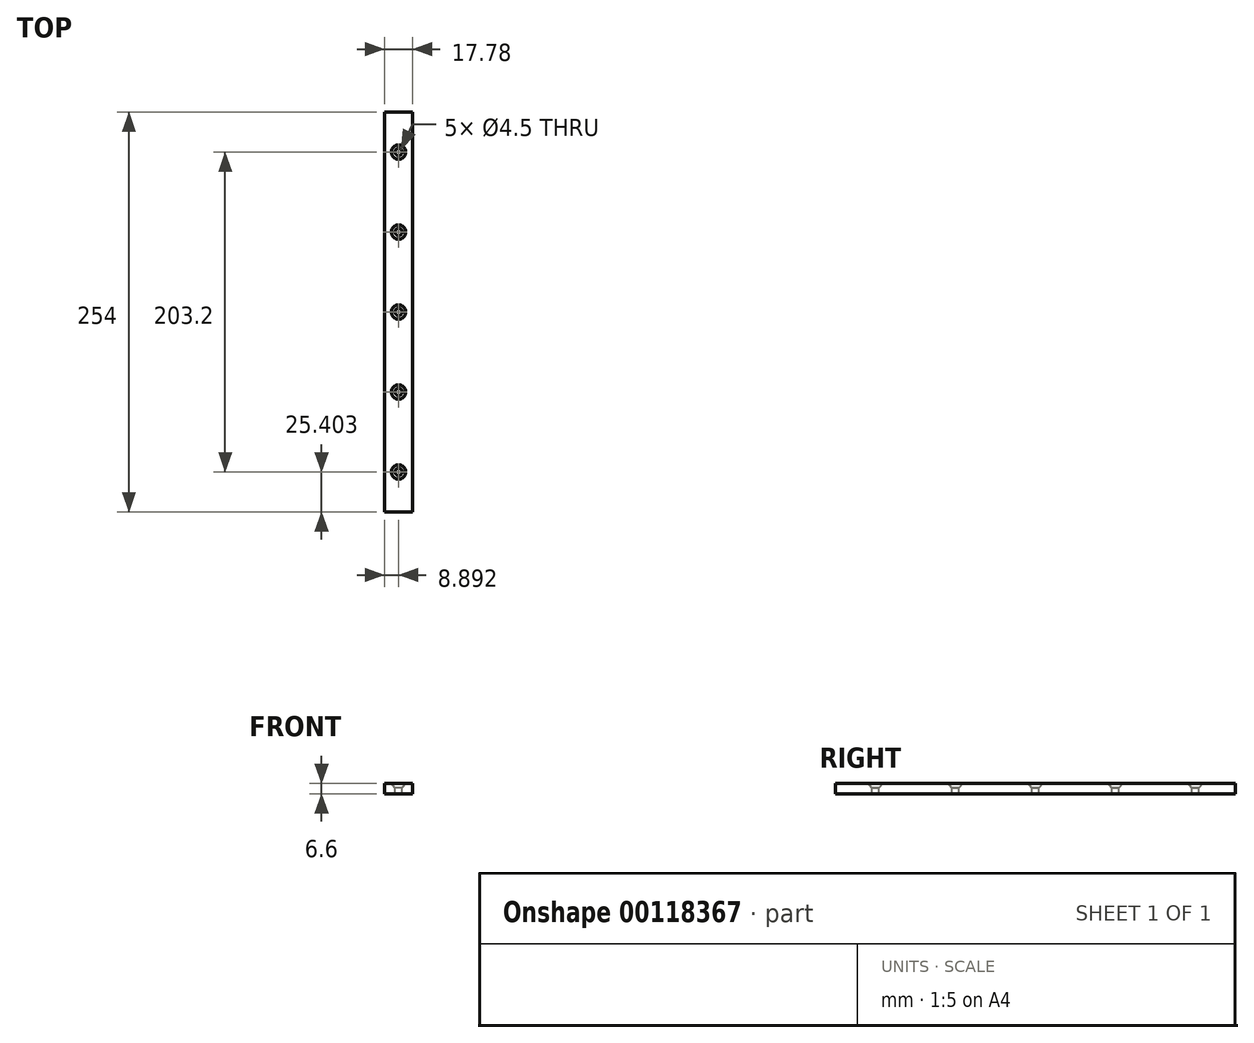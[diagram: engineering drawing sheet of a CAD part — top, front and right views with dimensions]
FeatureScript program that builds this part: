
annotation { "Feature Type Name" : "Feature", "Feature Type Description" : "" }
export const myFeature = defineFeature(function(context is Context, id is Id, definition is map)
    precondition{}
    {
        {
            var Q0;
            Q0=qCreatedBy(makeId("Top.planeOp"),FACE);
            var sketch = newSketch(context, id + "F0", { "sketchPlane" : qUnion([Q0])});
            skLineSegment(sketch, "E0.bottom", {"start": v(-5.89, 167.12) * mm, "end": v(11.9, 167.12) * mm});
            skLineSegment(sketch, "E0.top", {"start": v(-5.89, -86.88) * mm, "end": v(11.9, -86.88) * mm});
            skLineSegment(sketch, "E0.left", {"start": v(-5.89, 167.12) * mm, "end": v(-5.89, -86.88) * mm});
            skLineSegment(sketch, "E0.right", {"start": v(11.9, 167.12) * mm, "end": v(11.9, -86.88) * mm});
            skPoint(sketch, "E1.cCircle.centerSnap0", {"position": v(3, 167.12) * mm});
            skPoint(sketch, "E2.0.midPoint", {"position": v(5.8, 105.13) * mm});
            skSolve(sketch);
        }
        {
            var Q0;
            Q0=makeQuery(id+"F0.imprint","IMPRINT",FACE,{"disambiguationData":[TD([[makeQuery(id+"F0.imprint","IMPRINT",EDGE,{"derivedFrom":sQuery(id+"F0.wireOp",EDGE,"E0.bottom")}),-1.0]])]});
            extrude(context, id + "F1", {"entities" : qUnion([Q0]), "depth" : 6.6 * mm});
        }
        {
            var Q0;
            Q0=makeQuery(id+"F1.opExtrude","CAP_FACE",FACE,{"disambiguationData":[OSD([sQuery(id+"F0.wireOp",EDGE,"E0.bottom"),sQuery(id+"F0.wireOp",EDGE,"E0.top"),sQuery(id+"F0.wireOp",EDGE,"E0.left"),sQuery(id+"F0.wireOp",EDGE,"E0.right"),sQuery(id+"F0.wireOp",EDGE,"E1.0"),sQuery(id+"F0.wireOp",EDGE,"E1.1"),sQuery(id+"F0.wireOp",EDGE,"E1.2"),sQuery(id+"F0.wireOp",EDGE,"E1.3"),sQuery(id+"F0.wireOp",EDGE,"E1.4"),sQuery(id+"F0.wireOp",EDGE,"E1.5"),sQuery(id+"F0.wireOp",EDGE,"E2.0"),sQuery(id+"F0.wireOp",EDGE,"E2.1"),sQuery(id+"F0.wireOp",EDGE,"E2.2"),sQuery(id+"F0.wireOp",EDGE,"E2.3"),sQuery(id+"F0.wireOp",EDGE,"E2.4"),sQuery(id+"F0.wireOp",EDGE,"E2.5")])],"isStart":false});
            var sketch = newSketch(context, id + "F2", { "sketchPlane" : qUnion([Q0])});
            skPoint(sketch, "E3", {"position": v(3, -61.48) * mm});
            skPoint(sketch, "E3.positionSnap0", {"position": v(3, -86.88) * mm});
            skPoint(sketch, "E4", {"position": v(3, -10.68) * mm});
            skPoint(sketch, "E5", {"position": v(3, 40.12) * mm});
            skPoint(sketch, "E6", {"position": v(3, 141.72) * mm});
            skPoint(sketch, "E7", {"position": v(3, 90.92) * mm});
            skSolve(sketch);
        }
        {
            var Q0;
            Q0=sQuery(id+"F2.wireOp",VERTEX,"E6");
            var Q1;
            Q1=sQuery(id+"F2.wireOp",VERTEX,"E7");
            var Q2;
            Q2=sQuery(id+"F2.wireOp",VERTEX,"E5");
            var Q3;
            Q3=sQuery(id+"F2.wireOp",VERTEX,"E4");
            var Q4;
            Q4=sQuery(id+"F2.wireOp",VERTEX,"E3");
            var Q5;
            Q5=makeQuery(id+"F1.opExtrude","SWEPT_BODY",BODY,{"disambiguationData":[OSD([sQuery(id+"F0.wireOp",EDGE,"E0.bottom"),sQuery(id+"F0.wireOp",EDGE,"E0.top"),sQuery(id+"F0.wireOp",EDGE,"E0.left"),sQuery(id+"F0.wireOp",EDGE,"E0.right"),sQuery(id+"F0.wireOp",EDGE,"E1.0"),sQuery(id+"F0.wireOp",EDGE,"E1.1"),sQuery(id+"F0.wireOp",EDGE,"E1.2"),sQuery(id+"F0.wireOp",EDGE,"E1.3"),sQuery(id+"F0.wireOp",EDGE,"E1.4"),sQuery(id+"F0.wireOp",EDGE,"E1.5"),sQuery(id+"F0.wireOp",EDGE,"E2.0"),sQuery(id+"F0.wireOp",EDGE,"E2.1"),sQuery(id+"F0.wireOp",EDGE,"E2.2"),sQuery(id+"F0.wireOp",EDGE,"E2.3"),sQuery(id+"F0.wireOp",EDGE,"E2.4"),sQuery(id+"F0.wireOp",EDGE,"E2.5")])]});
            hole(context, id + "F3", {"style" : HoleStyle.C_SINK, "endStyle" : HoleEndStyle.THROUGH, "standardTappedOrClearance" : lookupTablePath({ "standard" : "ANSI", "fit" : "Normal (ASME)", "size" : "#8", "type" : "Clearance" }), "standardBlindInLast" : lookupTablePath({ "fit" : "Free", "standard" : "ANSI", "size" : "#8", "type" : "Clearance" }), "holeDiameter" : 4.5 * mm, "cSinkDiameter" : 9.12 * mm, "cSinkAngle" : 82 * degree, "locations" : qUnion([Q0, Q1, Q2, Q3, Q4]), "scope" : qUnion([Q5]), "isTappedThrough" : true});
        }
    });
